# Revit family: lp-750x4-60_60Hz
name_source: partatom
category: 機械設備
units: mm (PartAtom-declared; Revit-internal decimal feet)

## family parameters
OmniClass タイトル = Heat Exchangers for Ventilation Air
OmniClass 番号 = 23.75.10.34.21
パーツ タイプ = 標準
ロード時にボイドで切り取り = いいえ
丸型コネクタ寸法 = 直径を使用
作業面ベース = いいえ
共有 = いいえ
常に垂直 = はい
部屋計算ポイント = はい

## types (1)
- LP-750X4-60
    Clearance Back = 0  [stored 0 ft]
    Clearance Bottom = 0  [stored 0 ft]
    Clearance Front = 0  [stored 0 ft]
    Clearance Left = 0  [stored 0 ft]
    Clearance Right = 700  [stored 2.29659 ft]
    Clearance Top = 0  [stored 0 ft]
    D1 = 2000  [stored 6.56168 ft]
    Depth = 2000  [stored 6.56168 ft]
    Duct_EA_H = 274  [stored 0.89895 ft]
    Duct_EA_W = 273  [stored 0.895669 ft]
    Duct_Height = 41  [stored 0.134514 ft]
    Duct_OA_D = 49  [stored 0.160761 ft]
    Duct_OA_H = 296  [stored 0.971129 ft]
    Duct_OA_W = 43  [stored 0.141076 ft]
    Duct_Pitch1 = 80  [stored 0.262467 ft]
    Duct_RA_D = 49  [stored 0.160761 ft]
    Duct_RA_H = 296  [stored 0.971129 ft]
    Duct_RA_W = 43  [stored 0.141076 ft]
    Duct_SA_H = 274  [stored 0.89895 ft]
    Duct_SA_W = 273  [stored 0.895669 ft]
    EAサイズ_D = 420  [stored 1.37795 ft]
    EAサイズ_W = 640  [stored 2.09974 ft]
    H1 = 90  [stored 0.295276 ft]
    Height = 2370  [stored 7.77559 ft]
    IfcExportAs = IfcAirToAirHeatRecoveryType
    IfcExportType = ROTARYWHEEL
    MAX静圧 = 385.0 Pa
    MAX風量 = 7500.0 m³/h
    MID静圧 = 0.0 Pa
    MID風量 = 0.0 m³/h
    MIN静圧 = 0.0 Pa
    MIN風量 = 0.0 m³/h
    OAサイズ_D = 420  [stored 1.37795 ft]
    OAサイズ_W = 1100
    OAダクト接続_変更1 = いいえ
    OAダクト接続_変更2 = いいえ
    OAダクト接続_変更3 = いいえ
    OAダクト接続_通常 = はい
    OmniClassCode = 23-27 23 19 11
    RAサイズ_D = 420  [stored 1.37795 ft]
    RAサイズ_W = 1100
    RAダクト接続_変更1 = いいえ
    RAダクト接続_変更2 = いいえ
    RAダクト接続_変更3 = いいえ
    RAダクト接続_通常 = はい
    SAサイズ_D = 420  [stored 1.37795 ft]
    SAサイズ_W = 640  [stored 2.09974 ft]
    URL = https://www.mitsubishielectric.co.jp
    Uniclass2015Code = Pr_60_60_36_88
    Uniclass2015Title = Thermal wheels
    Uniclass2015Version = Systems v1.9
    W1 = 1180  [stored 3.87139 ft]
    Width = 1218  [stored 3.99606 ft]
    エンタルピ交換効率_冷房 = 60.00%
    エンタルピ交換効率_暖房 = 66.00%
    メンテナンススペース = はい
    モデル = LP-750X4-60
    仕様書バージョン = Version1.0
    企業コード = 108420
    価格 = 8091000 $
    分類コード = 50052504100050
    初期抵抗 = 0.0 Pa
    周波数 = 60 Hz
    呼称 = 全熱交換ユニット
    外気量 = 0.0 m³/h
    実風量 = 0.0 m³/h
    形式 = 床置形
    排気量 = 0.0 m³/h
    本体マテリアル = 溶融亜鉛めっき鋼板
    本体固定用穴_径 = 20  [stored 0.0656168 ft]
    本体固定用穴ピッチ1 = 1930  [stored 6.33202 ft]
    本体固定用穴ピッチ2 = 565  [stored 1.85367 ft]
    極数 = 3
    機外静圧 = 385.0 Pa
    機外静圧_排気 = 385.0 Pa
    法定耐用年数 = 15
    消費電力 = 7000 W
    温度交換効率 = 77.00%
    相 = 3
    積算_科目 = 1 空気調和設備
    符号 = HEU
    製品リリース年月 = 2018/7/25
    製品出荷対象 = 国内
    製品質量 = 835.00 kg
    製造元 = 三菱電機株式会社
    設置方法 = 床置形
    設計風量 = 0.0 m³/h
    説明 = 設備用ロスナイ ビル用ロスナイパック形
    負荷分類 = 3_ファン類
    質量 = 1002.00 kg
    運転質量 = 0.00 kg
    電動機出力 = 4 W
    電圧 = 200 V
    面風速 = 7.8 m/s
    風量 = 7500.0 m³/h
    騒音レベル(dB(A)) = 58.5

note: [stored X ft] marks values corroborated as IEEE doubles in the binary element streams (Revit-internal decimal feet)

## geometry (parser evidence)
native form markers: Blend x2
no freeform markers — native parametric forms only
